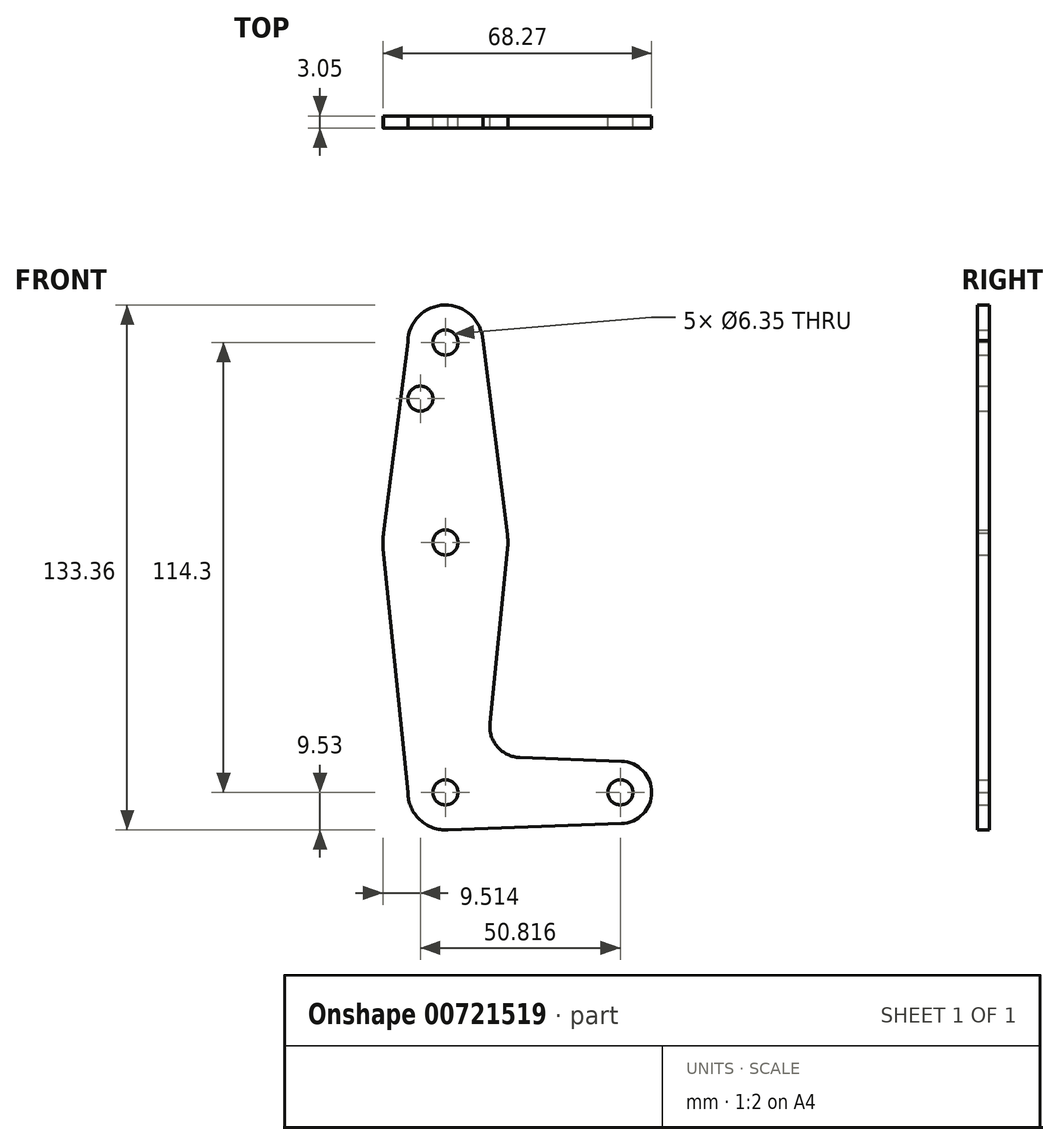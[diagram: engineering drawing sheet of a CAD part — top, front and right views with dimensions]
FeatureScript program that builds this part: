
annotation { "Feature Type Name" : "Feature", "Feature Type Description" : "" }
export const myFeature = defineFeature(function(context is Context, id is Id, definition is map)
    precondition{}
    {
        {
            var Q0;
            Q0=qCreatedBy(makeId("Front.planeOp"),FACE);
            var sketch = newSketch(context, id + "F0", { "sketchPlane" : qUnion([Q0])});
            skLineSegment(sketch, "E0", {"start": v(0, 0) * mm, "end": v(0, 114.3) * mm, "construction": true});
            skLineSegment(sketch, "E1", {"start": v(0, 0) * mm, "end": v(44.45, 0) * mm, "construction": true});
            skCircle(sketch, "E2", {"center": v(0, 114.3) * mm, "radius": 9.53 * mm});
            skCircle(sketch, "E3", {"center": v(0, 0) * mm, "radius": 9.53 * mm});
            skCircle(sketch, "E4", {"center": v(44.45, 0) * mm, "radius": 7.94 * mm});
            skCircle(sketch, "E5", {"center": v(0, 63.5) * mm, "radius": 15.88 * mm});
            skLineSegment(sketch, "E6", {"start": v(-9.53, 0) * mm, "end": v(-15.8, 61.9) * mm});
            skLineSegment(sketch, "E7", {"start": v(-9.52, 114.43) * mm, "end": v(-15.8, 65.1) * mm});
            skLineSegment(sketch, "E8", {"start": v(9.51, 114.77) * mm, "end": v(15.75, 65.5) * mm});
            skLineSegment(sketch, "E9", {"start": v(11.3, 17.6) * mm, "end": v(15.8, 61.9) * mm});
            skLineSegment(sketch, "E10", {"start": v(18.93, 8.85) * mm, "end": v(44.73, 7.93) * mm});
            skLineSegment(sketch, "E11", {"start": v(0, -9.53) * mm, "end": v(44.73, -7.93) * mm});
            skCircle(sketch, "E12", {"center": v(0, 114.3) * mm, "radius": 3.18 * mm});
            skCircle(sketch, "E13", {"center": v(0, 63.5) * mm, "radius": 3.18 * mm});
            skCircle(sketch, "E14", {"center": v(0, 0) * mm, "radius": 3.18 * mm});
            skCircle(sketch, "E15", {"center": v(44.45, 0) * mm, "radius": 3.18 * mm});
            skCircle(sketch, "E16", {"center": v(-6.37, 100.03) * mm, "radius": 3.18 * mm});
            skArc(sketch, "E17.filletArc", {"start": v(11.3, 17.6) * mm, "mid": v(13.22, 11.57) * mm, "end": v(18.93, 8.85) * mm});
            skSolve(sketch);
        }
        {
            var Q0;
            Q0 = qSketchRegion(id + "F0", true);
            extrude(context, id + "F1", {"entities" : qUnion([Q0]), "depth" : 3.05 * mm, "offsetDistance" : 25.4 * mm});
        }
    });
